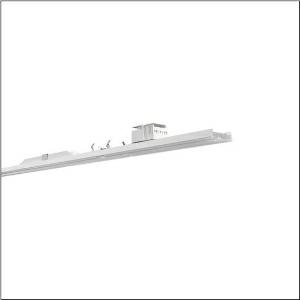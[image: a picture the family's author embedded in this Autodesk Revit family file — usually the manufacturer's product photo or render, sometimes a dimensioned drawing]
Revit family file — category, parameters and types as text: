
# Revit family: licross_r__11_recessed_mo_51tl19dv4e5f_7c8d
name_source: partatom
category: Lighting Fixtures
units: mm (PartAtom-declared; Revit-internal decimal feet)

## family parameters
Cut with Voids When Loaded = No
Host = Face
Light Source = No
Part Type = Normal
Room Calculation Point = No
Round Connector Dimension = Use Diameter
Shared = No

## types (1)
- --- (1 x LED, 14780 lm, 89.6 W, 4000K)
    Apparent Load = 90 VA
    CIE Flux Codes = 55 90 98 100 100
    Color Rendering = 80
    Color Temperature = 4000K
    Default Elevation = 1800 mm
    Description = Licross® 11 Recessed MOluminaire insert, length: 2.250mm, width: 66mm, height: 67mm, LED rated luminous flux: 14.780lm, light colour: 840, control gear: DALI 2, control gear: ECG DALI, with plug, 5-pole, with phase selection, mains connection: 220..240V, AC, 50/60Hz, halogen-free wiring, primary light control with lens, of plastic, primary optical cover: cover, of PMMA, light emission: direct distribution, primary light characteristic: double asymmetric, protection rating (complete): IP40, insulation class (complete): insulation class I (protective earthing), certification: CE, ENEC, VDE, protection symbol: D if used in an environment without relevant dust loads with corresponding accessories, permissible ambient temperature for indoor applications: -25..+35°C, corresponds to IFS (International Featured Standards) requirements for safety and quality in the food industry, reducing of maximum allowable ambient temperature of 5°C with ceiling mounting, packaging unit: 1 piece
    Height = 58 mm
    Lamp = 1 x LED
    Lamp Light Flux = 14780 lm
    Lamp Power = 89.6 W
    Lamp count = 1
    Length = 2250 mm
    Luminous efficacy = 165 lm/W
    Manufacturer = Siteco
    ModVariant = No
    Model = 51TL19DV4E5F
    Mounting Place = Ceiling
    Mounting Type = Pendant
    Number of Poles = 1
    OnlyDefault = Yes
    Power Factor = 1
    Product Name = Licross® 11 Recessed MO
    Product group = luminaire insert
    ProductGroupID = 902
    Protection Class = Protection class I
    Protection Degree = IP 40
    RLX_Detail_Level = 1
    RlxData = <blob elided: 27441 chars, md5=d38139e9>
    Socket = socket
    Standby Power = 0 W
    System Light Flux = 14780 lm
    System Power = 90 W
    Type Comments = factory setting: luminous flux: 100 % | dim-lin: 254 | 400 mA
    Type Image = l_1266722.jpg
    URL = http://relux.com
    VarID = @adj_133372
    Voltage = 0 V
    Weight = 0.00 kg
    Width = 66 mm

## geometry (parser evidence)
native form markers: Blend x4, Sweep x10
no freeform markers — native parametric forms only
